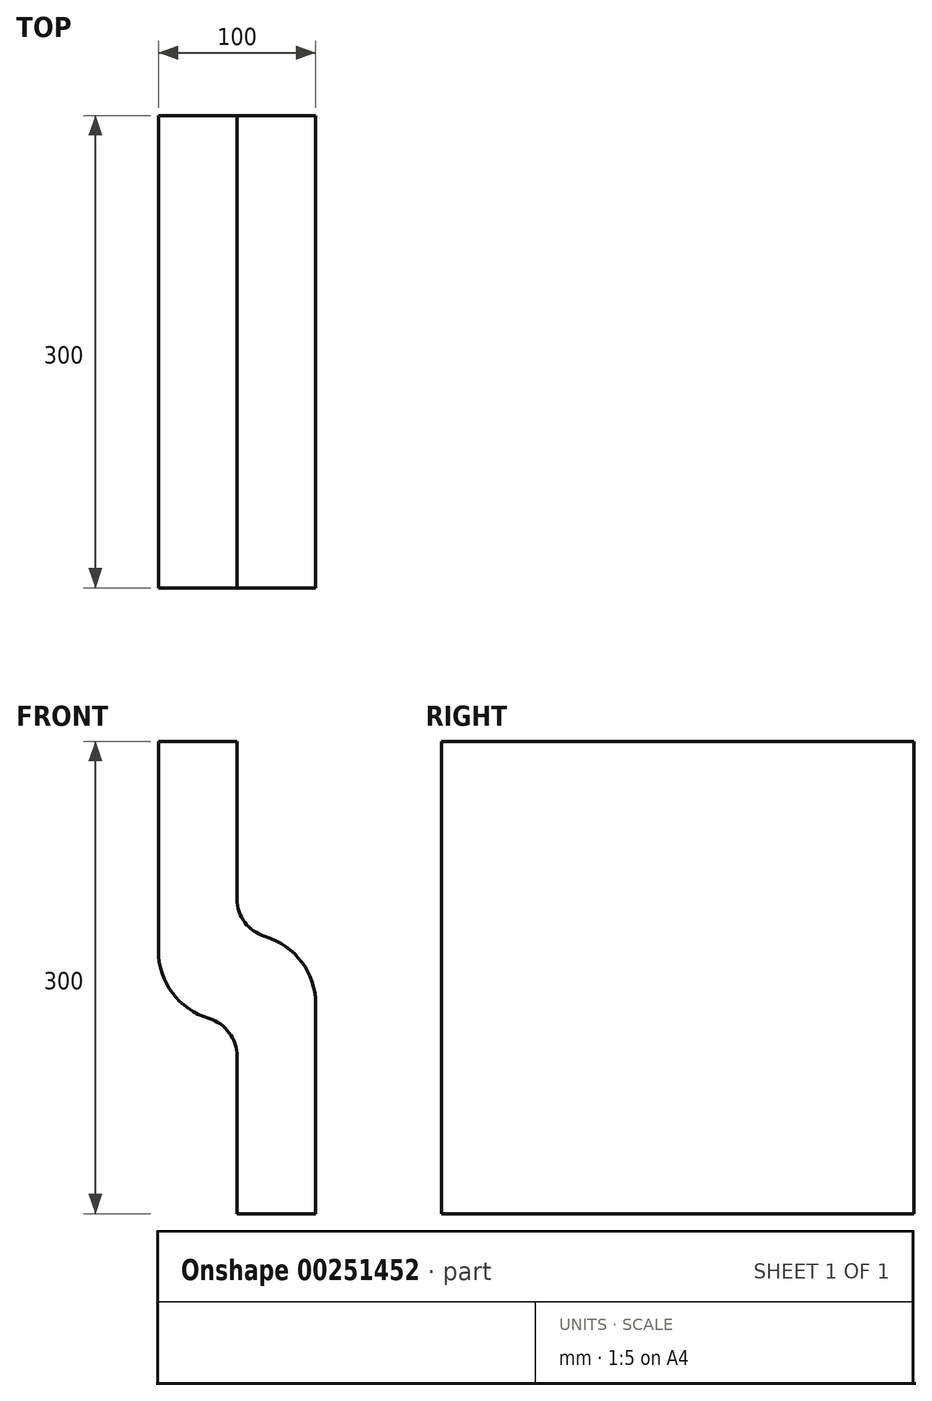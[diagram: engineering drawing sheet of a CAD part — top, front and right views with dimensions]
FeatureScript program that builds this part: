
annotation { "Feature Type Name" : "Feature", "Feature Type Description" : "" }
export const myFeature = defineFeature(function(context is Context, id is Id, definition is map)
    precondition{}
    {
        {
            var Q0;
            Q0=qCreatedBy(makeId("Front.planeOp"),FACE);
            var sketch = newSketch(context, id + "F0", { "sketchPlane" : qUnion([Q0])});
            skLineSegment(sketch, "E0", {"start": v(-47.12, 125) * mm, "end": v(-47.12, 0) * mm});
            skLineSegment(sketch, "E1", {"start": v(-47.12, 0) * mm, "end": v(2.88, 0) * mm});
            skLineSegment(sketch, "E2", {"start": v(2.88, 0) * mm, "end": v(2.88, -175) * mm});
            skLineSegment(sketch, "E3.0", {"start": v(-47.12, -50) * mm, "end": v(-47.12, -175) * mm});
            skLineSegment(sketch, "E3.1", {"start": v(-97.12, -50) * mm, "end": v(-47.12, -50) * mm});
            skLineSegment(sketch, "E3.2", {"start": v(-97.12, 125) * mm, "end": v(-97.12, -50) * mm});
            skLineSegment(sketch, "E4", {"start": v(-97.12, 125) * mm, "end": v(-47.12, 125) * mm});
            skLineSegment(sketch, "E5", {"start": v(-47.12, -175) * mm, "end": v(2.88, -175) * mm});
            skSolve(sketch);
        }
        {
            var Q0;
            Q0=makeQuery(id+"F0.imprint","IMPRINT",FACE,{"disambiguationData":[TD([[makeQuery(id+"F0.imprint","IMPRINT",EDGE,{"derivedFrom":sQuery(id+"F0.wireOp",EDGE,"E0")}),-1.0]])]});
            extrude(context, id + "F1", {"entities" : qUnion([Q0]), "depth" : 300 * mm});
        }
        {
            var Q0;
            Q0=makeQuery(id+"F1.opExtrude","SWEPT_EDGE",EDGE,{"disambiguationData":[OSD([sQuery(id+"F0.wireOp",EDGE,"E0"),sQuery(id+"F0.wireOp",EDGE,"E1")])]});
            var Q1;
            Q1=makeQuery(id+"F1.opExtrude","SWEPT_EDGE",EDGE,{"disambiguationData":[OSD([sQuery(id+"F0.wireOp",EDGE,"E3.0"),sQuery(id+"F0.wireOp",EDGE,"E3.1")])]});
            fillet(context, id + "F2", {"entities" : qUnion([Q0, Q1]), "radius" : 25 * mm, "tangentPropagation" : true, "allowEdgeOverflow" : false});
        }
        {
            var Q0;
            Q0=makeQuery(id+"F1.opExtrude","SWEPT_EDGE",EDGE,{"disambiguationData":[OSD([sQuery(id+"F0.wireOp",EDGE,"E1"),sQuery(id+"F0.wireOp",EDGE,"E2")])]});
            var Q1;
            Q1=makeQuery(id+"F1.opExtrude","SWEPT_EDGE",EDGE,{"disambiguationData":[OSD([sQuery(id+"F0.wireOp",EDGE,"E3.1"),sQuery(id+"F0.wireOp",EDGE,"E3.2")])]});
            fillet(context, id + "F3", {"entities" : qUnion([Q0, Q1]), "radius" : 45 * mm, "tangentPropagation" : true, "allowEdgeOverflow" : false});
        }
    });
